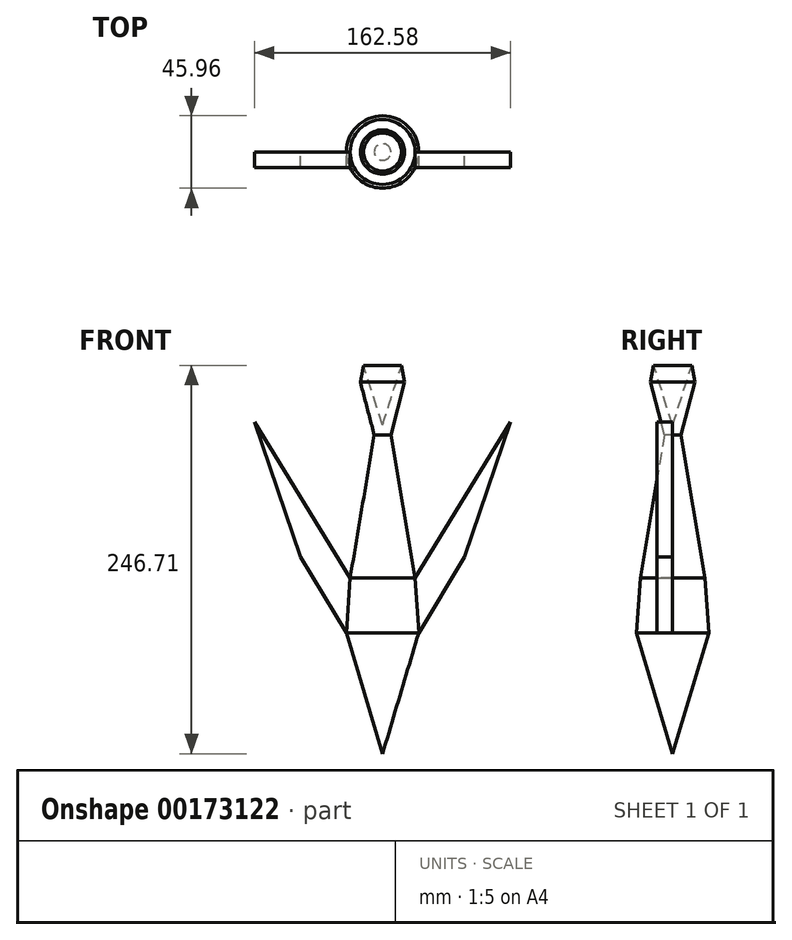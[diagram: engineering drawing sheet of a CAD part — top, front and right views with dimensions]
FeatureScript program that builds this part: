
annotation { "Feature Type Name" : "Feature", "Feature Type Description" : "" }
export const myFeature = defineFeature(function(context is Context, id is Id, definition is map)
    precondition{}
    {
        {
            var Q0;
            Q0=qCreatedBy(makeId("Front.planeOp"),FACE);
            var sketch = newSketch(context, id + "F0", { "sketchPlane" : qUnion([Q0])});
            skLineSegment(sketch, "E0", {"start": v(0, 76.58) * mm, "end": v(12.08, 114.53) * mm});
            skLineSegment(sketch, "E1", {"start": v(12.08, 114.53) * mm, "end": v(14.06, 103.77) * mm});
            skLineSegment(sketch, "E2", {"start": v(14.06, 103.77) * mm, "end": v(5.28, 70.35) * mm});
            skLineSegment(sketch, "E3", {"start": v(5.28, 70.35) * mm, "end": v(20.58, -20.57) * mm});
            skLineSegment(sketch, "E4", {"start": v(20.58, -20.57) * mm, "end": v(22.98, -55.4) * mm});
            skLineSegment(sketch, "E5", {"start": v(22.98, -55.4) * mm, "end": v(0, -132.18) * mm});
            skLineSegment(sketch, "E6", {"start": v(0, -132.18) * mm, "end": v(0, 0) * mm});
            skLineSegment(sketch, "E7", {"start": v(20.58, -20.57) * mm, "end": v(81.29, 78.64) * mm});
            skLineSegment(sketch, "E8", {"start": v(81.29, 78.64) * mm, "end": v(51.98, -7.25) * mm});
            skLineSegment(sketch, "E9", {"start": v(51.98, -7.25) * mm, "end": v(22.98, -55.4) * mm});
            skLineSegment(sketch, "E10", {"start": v(0, 76.58) * mm, "end": v(0, 0) * mm});
            skSolve(sketch);
        }
        {
            var Q0;
            Q0=makeQuery(id+"F0.imprint","IMPRINT",FACE,{"disambiguationData":[TD([[makeQuery(id+"F0.imprint","IMPRINT",EDGE,{"derivedFrom":sQuery(id+"F0.wireOp",EDGE,"E4")}),1.0]])]});
            extrude(context, id + "F1", {"entities" : qUnion([Q0]), "depth" : 10 * mm});
        }
        {
            var Q0;
            Q0=makeQuery(id+"F1.opExtrude","SWEPT_BODY",BODY,{"disambiguationData":[OSD([sQuery(id+"F0.wireOp",EDGE,"E4"),sQuery(id+"F0.wireOp",EDGE,"E7"),sQuery(id+"F0.wireOp",EDGE,"E8"),sQuery(id+"F0.wireOp",EDGE,"E9")])]});
            var Q1;
            Q1=qCreatedBy(makeId("Right.planeOp"),FACE);
            mirror(context, id + "F2", {"entities" : qUnion([Q0]), "mirrorPlane" : qUnion([Q1])});
        }
        {
            var Q0;
            Q0=makeQuery(id+"F0.imprint","IMPRINT",FACE,{"disambiguationData":[TD([[makeQuery(id+"F0.imprint","IMPRINT",EDGE,{"derivedFrom":sQuery(id+"F0.wireOp",EDGE,"E0")}),-1.0]])]});
            var Q1;
            Q1=sQuery(id+"F0.wireOp",EDGE,"E6");
            revolve(context, id + "F3", {"entities" : qUnion([Q0]), "axis" : qUnion([Q1]), "revolveType" : RevolveType.FULL});
        }
    });
